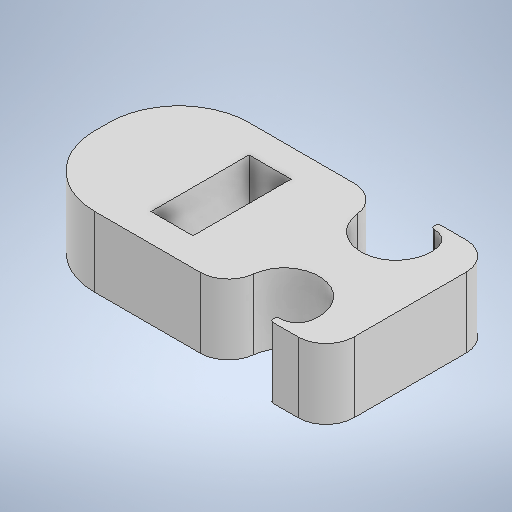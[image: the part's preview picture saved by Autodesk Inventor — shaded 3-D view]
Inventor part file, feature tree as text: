
AUTODESK INVENTOR PART (.ipt)
format: ipt  version: 2025.2 (Build 292293000, 293)  size: 327,168 bytes
history: native  units: in
note: dims shown in document units (in); Inventor stores cm internally (conversion verified against a paired STEP export)
features: fillet x12, extrude x5, sketch x5
ambient origin geometry x8: Origin, YZ Plane, XZ Plane, XY Plane, X Axis, Y Axis, Z Axis, Center Point
bodies: Solid1 (feature_tree)
feature tree (22):
  extrude  "Extrusion1"  Depth=0.4331in
  extrude  "Extrusion2"  Depth=0.1969in
  fillet  "Fillet1"  Radius=0.1969in
  fillet  "Fillet2"  Radius=0.0591in
  fillet  "Fillet3"  Radius=0.0591in
  fillet  "Fillet4"  Radius=0.1969in
  extrude  "Extrusion3"  Depth=0.0787in
  fillet  "Fillet5"  Radius=0.1969in
  fillet  "Fillet6"  Radius=0.1969in
  fillet  "Fillet7"  Radius=0.1969in
  fillet  "Fillet8"  Radius=0.1969in
  fillet  "Fillet9"  Radius=0.1575in
  fillet  "Fillet10"  Radius=0.0197in
  fillet  "Fillet11"  Radius=0.1575in
  fillet  "Fillet12"  Radius=0.0197in
  extrude  "Extrusion4"  Depth=0.1969in
  extrude  "Extrusion5"  Depth=0.3937in
  sketch  "Sketch1"  dims[d0=0.8661in d1=0.4331in]
  sketch  "Sketch2"  dims[d2=0.1969in d3=0.0in d4=0.1969in d5=0.1969in d6=0.0591in d7=0.0591in d8=0.1969in d9=0.0in]
  sketch  "Sketch3"  dims[d10=0.0787in d11=0.0787in d12=0.1969in d13=0.1969in d14=0.1969in d15=0.1969in d16=0.1575in d17=0.0197in d18=0.1575in d19=0.0197in]
  sketch  "Sketch4"  dims[d20=0.1969in d21=0.0in d22=0.0472in]
  sketch  "Sketch5"  dims[d23=0.0472in d24=0.0079in d25=0.0079in d26=0.0079in d27=0.0079in d28=0.0787in d29=0.0787in d30=0.1299in d31=0.2165in d33=0.2165in d34=0.1969in d35=0.0in d36=0.0787in d37=0.0787in d38=0.2756in d39=0.1181in d40=0.3937in d41=0.0in d42=0.0197in d43=0.0344in]
